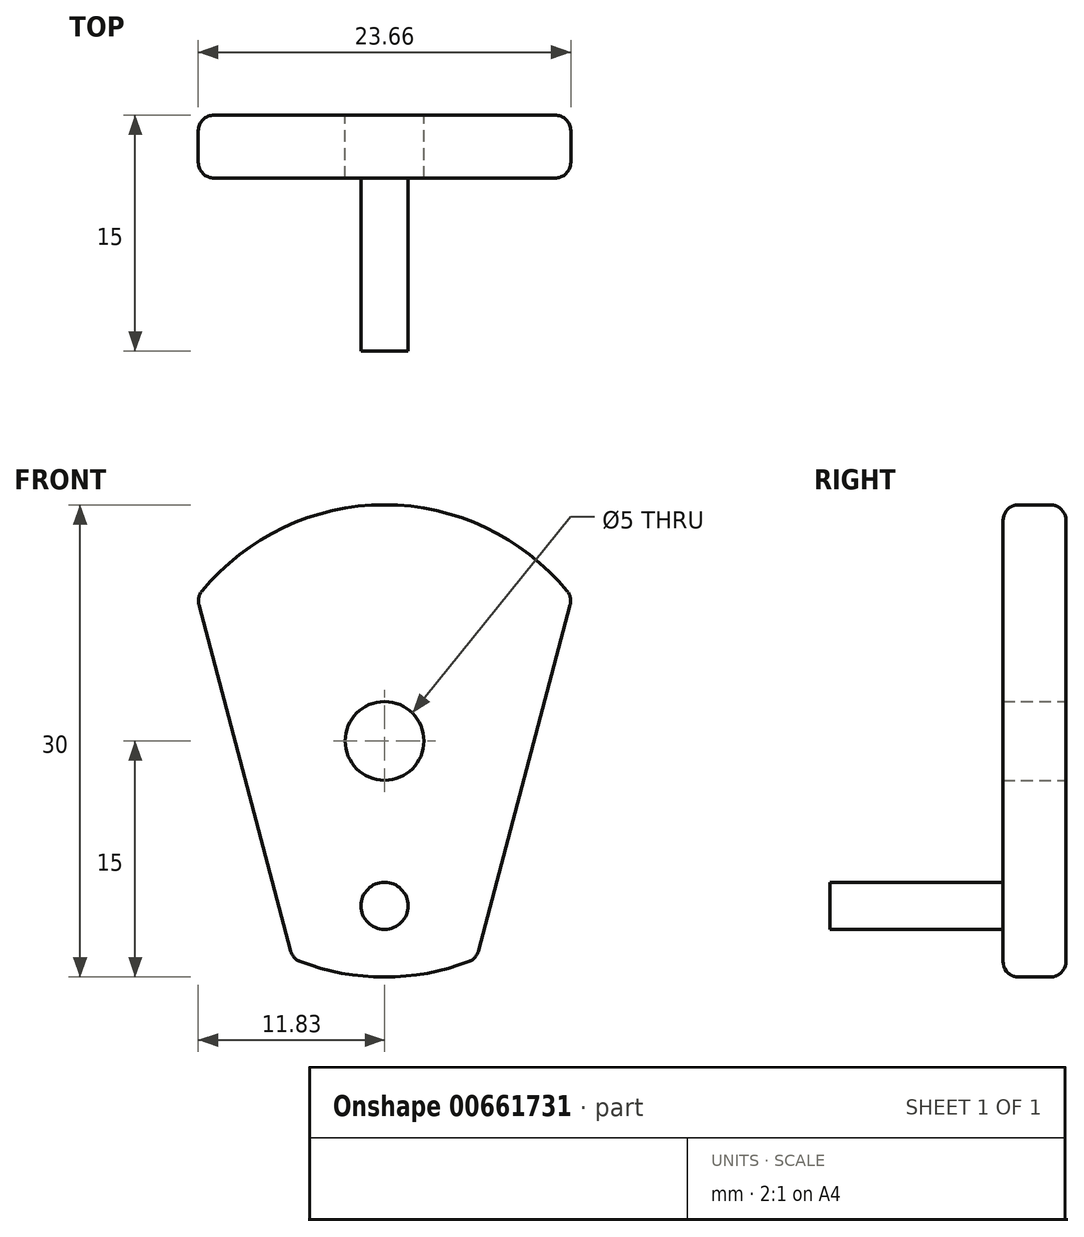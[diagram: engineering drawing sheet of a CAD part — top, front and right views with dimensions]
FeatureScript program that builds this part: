
annotation { "Feature Type Name" : "Feature", "Feature Type Description" : "" }
export const myFeature = defineFeature(function(context is Context, id is Id, definition is map)
    precondition{}
    {
        {
            var Q0;
            Q0=qCreatedBy(makeId("Front.planeOp"),FACE);
            var sketch = newSketch(context, id + "F0", { "sketchPlane" : qUnion([Q0])});
            skArc(sketch, "E0", {"start": v(-5.85, -13.81) * mm, "mid": v(0, -15) * mm, "end": v(5.85, -13.81) * mm});
            skLineSegment(sketch, "E1", {"start": v(-11.92, 9.1) * mm, "end": v(-5.85, -13.81) * mm});
            skLineSegment(sketch, "E2.MirrorCS", {"start": v(11.92, 9.1) * mm, "end": v(5.85, -13.81) * mm});
            skArc(sketch, "E3.trimOffspring", {"start": v(11.92, 9.1) * mm, "mid": v(0, 15) * mm, "end": v(-11.92, 9.1) * mm});
            skCircle(sketch, "E4", {"center": v(0, -10.48) * mm, "radius": 1.5 * mm});
            skSolve(sketch);
        }
        {
            var Q0;
            Q0=makeQuery(id+"F0.imprint","IMPRINT",FACE,{"disambiguationData":[TD([[makeQuery(id+"F0.imprint","IMPRINT",EDGE,{"derivedFrom":sQuery(id+"F0.wireOp",EDGE,"E4")}),1.0]])]});
            extrude(context, id + "F1", {"entities" : qUnion([Q0]), "depth" : 15 * mm, "offsetDistance" : 25 * mm});
        }
        {
            var Q0;
            Q0 = qSketchRegion(id + "F0", true);
            extrude(context, id + "F2", {"entities" : qUnion([Q0]), "operationType" : NewBodyOperationType.ADD, "depth" : 4 * mm, "offsetDistance" : 25 * mm});
        }
        {
            var Q0;
            {var subQ0=sQuery(id+"F0.wireOp",EDGE,"E4");Q0=makeQuery(id+"F2.boolean.opBoolean","MERGE",FACE,{"derivedFrom":[makeQuery(id+"F1.opExtrude","CAP_FACE",FACE,{"disambiguationData":[OSD([subQ0])],"isStart":true}),makeQuery(id+"F2.opExtrude","CAP_FACE",FACE,{"disambiguationData":[OSD([sQuery(id+"F0.wireOp",EDGE,"E0"),sQuery(id+"F0.wireOp",EDGE,"E1"),sQuery(id+"F0.wireOp",EDGE,"E2.MirrorCS"),sQuery(id+"F0.wireOp",EDGE,"E3.trimOffspring"),subQ0])],"isStart":true})]});}
            var sketch = newSketch(context, id + "F3", { "sketchPlane" : qUnion([Q0])});
            skCircle(sketch, "E5", {"center": v(0, 0) * mm, "radius": 2.5 * mm});
            skSolve(sketch);
        }
        {
            var Q0;
            Q0 = qSketchRegion(id + "F3", true);
            extrude(context, id + "F4", {"entities" : qUnion([Q0]), "operationType" : NewBodyOperationType.REMOVE, "oppositeDirection" : true, "depth" : 25 * mm, "offsetDistance" : 25 * mm});
        }
        {
            var Q0;
            Q0=makeQuery(id+"F2.opExtrude","CAP_EDGE",EDGE,{"disambiguationData":[OSD([sQuery(id+"F0.wireOp",EDGE,"E3.trimOffspring")])],"isStart":false});
            var Q1;
            Q1=makeQuery(id+"F2.opExtrude","SWEPT_EDGE",EDGE,{"disambiguationData":[OSD([sQuery(id+"F0.wireOp",EDGE,"E2.MirrorCS"),sQuery(id+"F0.wireOp",EDGE,"E3.trimOffspring")])]});
            var Q2;
            Q2=makeQuery(id+"F2.opExtrude","SWEPT_EDGE",EDGE,{"disambiguationData":[OSD([sQuery(id+"F0.wireOp",EDGE,"E1"),sQuery(id+"F0.wireOp",EDGE,"E3.trimOffspring")])]});
            var Q3;
            Q3=makeQuery(id+"F2.opExtrude","CAP_EDGE",EDGE,{"disambiguationData":[OSD([sQuery(id+"F0.wireOp",EDGE,"E3.trimOffspring")])],"isStart":true});
            var Q4;
            Q4=makeQuery(id+"F2.opExtrude","SWEPT_EDGE",EDGE,{"disambiguationData":[OSD([sQuery(id+"F0.wireOp",EDGE,"E0"),sQuery(id+"F0.wireOp",EDGE,"E2.MirrorCS")])]});
            var Q5;
            Q5=makeQuery(id+"F2.opExtrude","CAP_EDGE",EDGE,{"disambiguationData":[OSD([sQuery(id+"F0.wireOp",EDGE,"E0")])],"isStart":false});
            var Q6;
            Q6=makeQuery(id+"F2.opExtrude","CAP_EDGE",EDGE,{"disambiguationData":[OSD([sQuery(id+"F0.wireOp",EDGE,"E0")])],"isStart":true});
            var Q7;
            Q7=makeQuery(id+"F2.opExtrude","SWEPT_EDGE",EDGE,{"disambiguationData":[OSD([sQuery(id+"F0.wireOp",EDGE,"E0"),sQuery(id+"F0.wireOp",EDGE,"E1")])]});
            var Q8;
            Q8=makeQuery(id+"F2.opExtrude","CAP_EDGE",EDGE,{"disambiguationData":[OSD([sQuery(id+"F0.wireOp",EDGE,"E1")])],"isStart":true});
            var Q9;
            Q9=makeQuery(id+"F2.opExtrude","CAP_EDGE",EDGE,{"disambiguationData":[OSD([sQuery(id+"F0.wireOp",EDGE,"E1")])],"isStart":false});
            var Q10;
            Q10=makeQuery(id+"F2.opExtrude","CAP_EDGE",EDGE,{"disambiguationData":[OSD([sQuery(id+"F0.wireOp",EDGE,"E2.MirrorCS")])],"isStart":false});
            var Q11;
            Q11=makeQuery(id+"F2.opExtrude","CAP_EDGE",EDGE,{"disambiguationData":[OSD([sQuery(id+"F0.wireOp",EDGE,"E2.MirrorCS")])],"isStart":true});
            fillet(context, id + "F5", {"entities" : qUnion([Q0, Q1, Q2, Q3, Q4, Q5, Q6, Q7, Q8, Q9, Q10, Q11]), "radius" : 1 * mm, "tangentPropagation" : true, "allowEdgeOverflow" : false});
        }
    });
